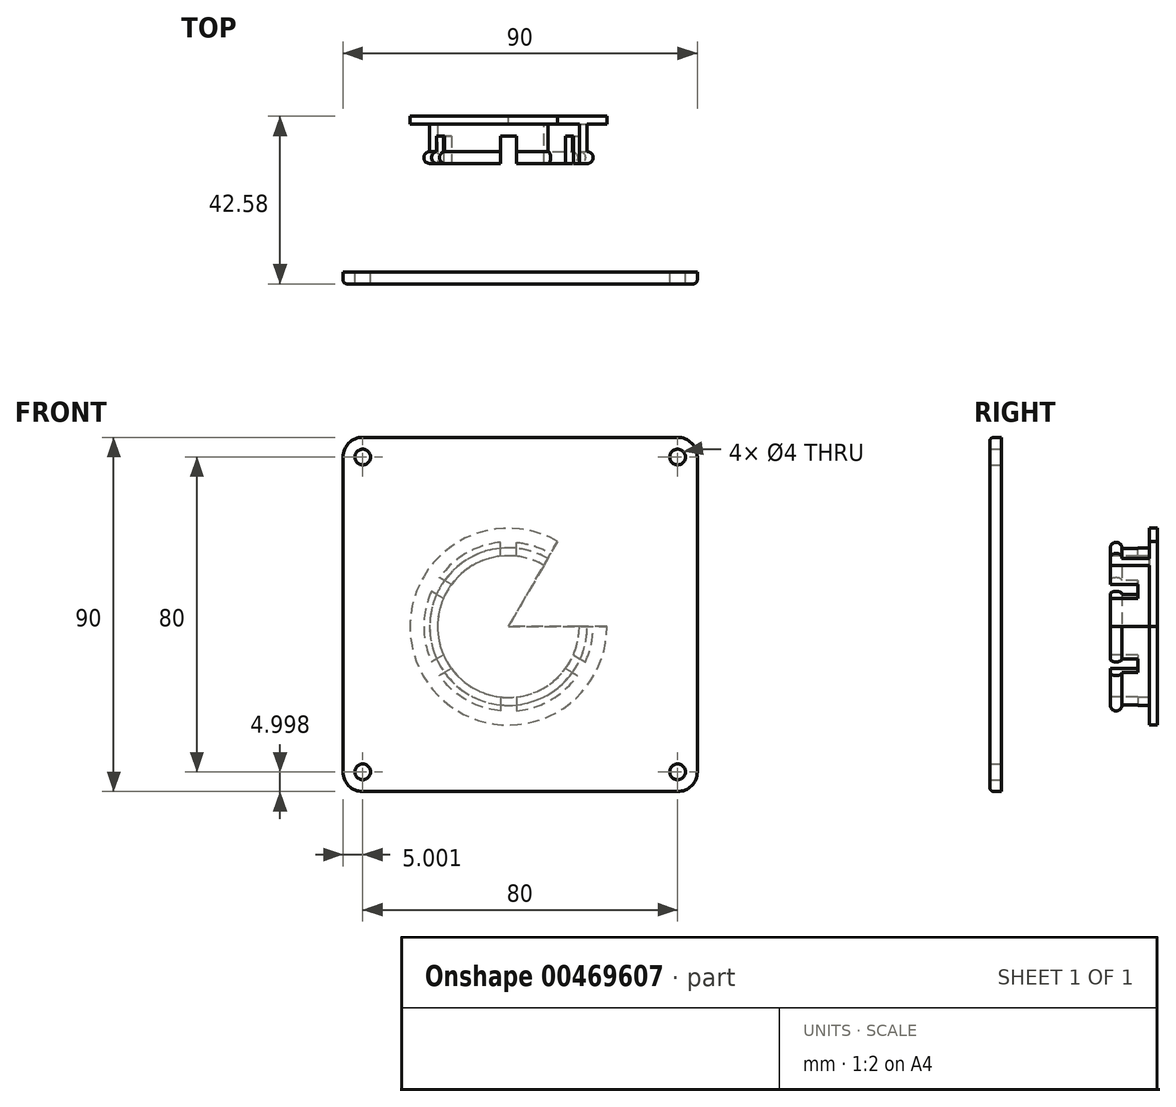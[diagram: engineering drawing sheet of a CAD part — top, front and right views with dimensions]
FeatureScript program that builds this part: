
annotation { "Feature Type Name" : "Feature", "Feature Type Description" : "" }
export const myFeature = defineFeature(function(context is Context, id is Id, definition is map)
    precondition{}
    {
        {
            var Q0;
            Q0=qCreatedBy(makeId("Front.planeOp"),FACE);
            var sketch = newSketch(context, id + "F0", { "sketchPlane" : qUnion([Q0])});
            skLineSegment(sketch, "E0.bottom", {"start": v(-37.02, 48.09) * mm, "end": v(42.98, 48.09) * mm});
            skLineSegment(sketch, "E0.top", {"start": v(-37.02, -41.91) * mm, "end": v(42.98, -41.91) * mm});
            skLineSegment(sketch, "E0.left", {"start": v(-42.02, 43.09) * mm, "end": v(-42.02, -36.91) * mm});
            skLineSegment(sketch, "E0.right", {"start": v(47.98, 43.09) * mm, "end": v(47.98, -36.91) * mm});
            skPoint(sketch, "E1.visualSharp", {"position": v(-42.02, 48.09) * mm});
            skArc(sketch, "E1.filletArc", {"start": v(-37.02, 48.09) * mm, "mid": v(-40.55, 46.62) * mm, "end": v(-42.02, 43.09) * mm});
            skPoint(sketch, "E2.visualSharp", {"position": v(47.98, 48.09) * mm});
            skArc(sketch, "E2.filletArc", {"start": v(47.98, 43.09) * mm, "mid": v(46.52, 46.62) * mm, "end": v(42.98, 48.09) * mm});
            skPoint(sketch, "E3.visualSharp", {"position": v(47.98, -41.91) * mm});
            skArc(sketch, "E3.filletArc", {"start": v(42.98, -41.91) * mm, "mid": v(46.52, -40.45) * mm, "end": v(47.98, -36.91) * mm});
            skPoint(sketch, "E4.visualSharp", {"position": v(-42.02, -41.91) * mm});
            skArc(sketch, "E4.filletArc", {"start": v(-42.02, -36.91) * mm, "mid": v(-40.55, -40.45) * mm, "end": v(-37.02, -41.91) * mm});
            skSolve(sketch);
        }
        {
            var Q0;
            Q0=makeQuery(id+"F0.imprint","IMPRINT",FACE,{"disambiguationData":[TD([[makeQuery(id+"F0.imprint","IMPRINT",EDGE,{"derivedFrom":sQuery(id+"F0.wireOp",EDGE,"E0.bottom")}),-1.0]])]});
            extrude(context, id + "F1", {"entities" : qUnion([Q0]), "depth" : 3 * mm});
        }
        {
            var Q0;
            Q0=makeQuery(id+"F1.opExtrude","CAP_FACE",FACE,{"disambiguationData":[OSD([sQuery(id+"F0.wireOp",EDGE,"E0.bottom"),sQuery(id+"F0.wireOp",EDGE,"E0.top"),sQuery(id+"F0.wireOp",EDGE,"E0.left"),sQuery(id+"F0.wireOp",EDGE,"E0.right"),sQuery(id+"F0.wireOp",EDGE,"E1.filletArc"),sQuery(id+"F0.wireOp",EDGE,"E2.filletArc"),sQuery(id+"F0.wireOp",EDGE,"E3.filletArc"),sQuery(id+"F0.wireOp",EDGE,"E4.filletArc")])],"isStart":false});
            fillet(context, id + "F2", {"entities" : qUnion([Q0]), "radius" : 1 * mm, "tangentPropagation" : true, "allowEdgeOverflow" : false});
        }
        {
            var Q0;
            Q0=sQuery(id+"F0.wireOp",VERTEX,"E2.filletArc.center");
            var Q1;
            Q1=sQuery(id+"F0.wireOp",VERTEX,"E3.filletArc.center");
            var Q2;
            Q2=sQuery(id+"F0.wireOp",VERTEX,"E4.filletArc.center");
            var Q3;
            Q3=sQuery(id+"F0.wireOp",VERTEX,"E1.filletArc.center");
            var Q4;
            Q4=makeQuery(id+"F1.opExtrude","SWEPT_BODY",BODY,{"disambiguationData":[OSD([sQuery(id+"F0.wireOp",EDGE,"E0.bottom"),sQuery(id+"F0.wireOp",EDGE,"E0.top"),sQuery(id+"F0.wireOp",EDGE,"E0.left"),sQuery(id+"F0.wireOp",EDGE,"E0.right"),sQuery(id+"F0.wireOp",EDGE,"E1.filletArc"),sQuery(id+"F0.wireOp",EDGE,"E2.filletArc"),sQuery(id+"F0.wireOp",EDGE,"E3.filletArc"),sQuery(id+"F0.wireOp",EDGE,"E4.filletArc")])]});
            hole(context, id + "F3", {"style" : HoleStyle.SIMPLE, "endStyle" : HoleEndStyle.THROUGH, "oppositeDirection" : true, "holeDiameter" : 4 * mm, "isTappedThrough" : true, "tappedDepth" : 12 * mm, "tapClearance" : 3, "locations" : qUnion([Q0, Q1, Q2, Q3]), "scope" : qUnion([Q4])});
        }
        {
            var Q0;
            Q0=qCreatedBy(makeId("Top.planeOp"),FACE);
            var sketch = newSketch(context, id + "F4", { "sketchPlane" : qUnion([Q0])});
            skLineSegment(sketch, "E5", {"start": v(0, 39.58) * mm, "end": v(25, 39.58) * mm});
            skLineSegment(sketch, "E6", {"start": v(25, 39.58) * mm, "end": v(25, 37.58) * mm});
            skLineSegment(sketch, "E7", {"start": v(25, 37.58) * mm, "end": v(20, 37.58) * mm});
            skLineSegment(sketch, "E8", {"start": v(20, 37.58) * mm, "end": v(20, 27.58) * mm});
            skLineSegment(sketch, "E9", {"start": v(20, 27.58) * mm, "end": v(18, 27.58) * mm});
            skLineSegment(sketch, "E10", {"start": v(18, 27.58) * mm, "end": v(18, 37.58) * mm});
            skLineSegment(sketch, "E11", {"start": v(18, 37.58) * mm, "end": v(0, 37.58) * mm});
            skLineSegment(sketch, "E12", {"start": v(0, 37.58) * mm, "end": v(0, 39.58) * mm});
            skArc(sketch, "E13", {"start": v(20, 27.58) * mm, "mid": v(21.5, 29.08) * mm, "end": v(20, 30.58) * mm});
            skSolve(sketch);
        }
        {
            var Q0;
            Q0=makeQuery(id+"F4.imprint","IMPRINT",FACE,{"disambiguationData":[TD([[makeQuery(id+"F4.imprint","IMPRINT",EDGE,{"derivedFrom":sQuery(id+"F4.wireOp",EDGE,"E5")}),-1.0]])]});
            var Q1;
            {var subQ0=sQuery(id+"F4.wireOp",EDGE,"E13");Q1=makeQuery(id+"F4.imprint","IMPRINT",FACE,{"disambiguationData":[TD([[makeQuery(id+"F4.imprint","IMPRINT",EDGE,{"derivedFrom":subQ0}),1.0]])]});}
            var Q2;
            Q2=sQuery(id+"F4.wireOp",EDGE,"E12");
            revolve(context, id + "F5", {"entities" : qUnion([Q0, Q1]), "axis" : qUnion([Q2]), "revolveType" : RevolveType.ONE_DIRECTION, "angle" : 300 * degree});
        }
        {
            var Q0;
            Q0=qCreatedBy(makeId("Top.planeOp"),FACE);
            cPlane(context, id + "F6", {"entities" : qUnion([Q0]), "cplaneType" : CPlaneType.OFFSET, "offset" : 25 * mm, "width" : 150 * mm, "height" : 150 * mm});
        }
        {
            var Q0;
            Q0=qCreatedBy(id+"F6.planeOp",FACE);
            var sketch = newSketch(context, id + "F7", { "sketchPlane" : qUnion([Q0])});
            skLineSegment(sketch, "E14.bottom", {"start": v(-2, 34.58) * mm, "end": v(2, 34.58) * mm});
            skLineSegment(sketch, "E14.top", {"start": v(-2, 27.58) * mm, "end": v(2, 27.58) * mm});
            skLineSegment(sketch, "E14.left", {"start": v(-2, 34.58) * mm, "end": v(-2, 27.58) * mm});
            skLineSegment(sketch, "E14.right", {"start": v(2, 34.58) * mm, "end": v(2, 27.58) * mm});
            skSolve(sketch);
        }
        {
            var Q0;
            Q0=makeQuery(id+"F7.imprint","IMPRINT",FACE,{"disambiguationData":[TD([[makeQuery(id+"F7.imprint","IMPRINT",EDGE,{"derivedFrom":sQuery(id+"F7.wireOp",EDGE,"E14.bottom")}),-1.0]])]});
            extrude(context, id + "F8", {"entities" : qUnion([Q0]), "oppositeDirection" : true, "depth" : 10 * mm});
        }
        {
            var Q0;
            Q0=makeQuery(id+"F8.opExtrude","SWEPT_BODY",BODY,{"disambiguationData":[OSD([sQuery(id+"F7.wireOp",EDGE,"E14.bottom"),sQuery(id+"F7.wireOp",EDGE,"E14.top"),sQuery(id+"F7.wireOp",EDGE,"E14.left"),sQuery(id+"F7.wireOp",EDGE,"E14.right")])]});
            var Q1;
            Q1=makeQuery(id+"F5.opRevolve","SWEPT_FACE",FACE,{"disambiguationData":[OSD([sQuery(id+"F4.wireOp",EDGE,"E8")])]});
            circularPattern(context, id + "F9", {"entities" : qUnion([Q0]), "axis" : qUnion([Q1]), "angle" : 360 * degree, "instanceCount" : 6, "equalSpace" : true});
        }
        {
            var Q0;
            Q0=makeQuery(id+"F9.opPattern","COPY",BODY,{"derivedFrom":makeQuery(id+"F8.opExtrude","SWEPT_BODY",BODY,{"disambiguationData":[OSD([sQuery(id+"F7.wireOp",EDGE,"E14.bottom"),sQuery(id+"F7.wireOp",EDGE,"E14.top"),sQuery(id+"F7.wireOp",EDGE,"E14.left"),sQuery(id+"F7.wireOp",EDGE,"E14.right")])]}),"instanceName":"2"});
            var Q1;
            Q1=makeQuery(id+"F9.opPattern","COPY",BODY,{"derivedFrom":makeQuery(id+"F8.opExtrude","SWEPT_BODY",BODY,{"disambiguationData":[OSD([sQuery(id+"F7.wireOp",EDGE,"E14.bottom"),sQuery(id+"F7.wireOp",EDGE,"E14.top"),sQuery(id+"F7.wireOp",EDGE,"E14.left"),sQuery(id+"F7.wireOp",EDGE,"E14.right")])]}),"instanceName":"1"});
            var Q2;
            Q2=makeQuery(id+"F8.opExtrude","SWEPT_BODY",BODY,{"disambiguationData":[OSD([sQuery(id+"F7.wireOp",EDGE,"E14.bottom"),sQuery(id+"F7.wireOp",EDGE,"E14.top"),sQuery(id+"F7.wireOp",EDGE,"E14.left"),sQuery(id+"F7.wireOp",EDGE,"E14.right")])]});
            var Q3;
            Q3=makeQuery(id+"F9.opPattern","COPY",BODY,{"derivedFrom":makeQuery(id+"F8.opExtrude","SWEPT_BODY",BODY,{"disambiguationData":[OSD([sQuery(id+"F7.wireOp",EDGE,"E14.bottom"),sQuery(id+"F7.wireOp",EDGE,"E14.top"),sQuery(id+"F7.wireOp",EDGE,"E14.left"),sQuery(id+"F7.wireOp",EDGE,"E14.right")])]}),"instanceName":"5"});
            var Q4;
            Q4=makeQuery(id+"F9.opPattern","COPY",BODY,{"derivedFrom":makeQuery(id+"F8.opExtrude","SWEPT_BODY",BODY,{"disambiguationData":[OSD([sQuery(id+"F7.wireOp",EDGE,"E14.bottom"),sQuery(id+"F7.wireOp",EDGE,"E14.top"),sQuery(id+"F7.wireOp",EDGE,"E14.left"),sQuery(id+"F7.wireOp",EDGE,"E14.right")])]}),"instanceName":"4"});
            var Q5;
            Q5=makeQuery(id+"F9.opPattern","COPY",BODY,{"derivedFrom":makeQuery(id+"F8.opExtrude","SWEPT_BODY",BODY,{"disambiguationData":[OSD([sQuery(id+"F7.wireOp",EDGE,"E14.bottom"),sQuery(id+"F7.wireOp",EDGE,"E14.top"),sQuery(id+"F7.wireOp",EDGE,"E14.left"),sQuery(id+"F7.wireOp",EDGE,"E14.right")])]}),"instanceName":"3"});
            var Q6;
            Q6=makeQuery(id+"F5.opRevolve","SWEPT_BODY",BODY,{"disambiguationData":[OSD([sQuery(id+"F4.wireOp",EDGE,"E5"),sQuery(id+"F4.wireOp",EDGE,"E6"),sQuery(id+"F4.wireOp",EDGE,"E7"),sQuery(id+"F4.wireOp",EDGE,"E8"),sQuery(id+"F4.wireOp",EDGE,"E9"),sQuery(id+"F4.wireOp",EDGE,"E10"),sQuery(id+"F4.wireOp",EDGE,"E11"),sQuery(id+"F4.wireOp",EDGE,"E12")])]});
            booleanBodies(context, id + "F10", {"operationType" : BooleanOperationType.SUBTRACTION, "tools" : qUnion([Q0, Q1, Q2, Q3, Q4, Q5]), "targets" : qUnion([Q6])});
        }
    });
